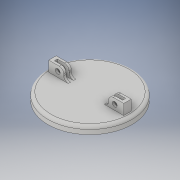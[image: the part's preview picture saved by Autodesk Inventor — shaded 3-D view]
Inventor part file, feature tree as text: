
AUTODESK INVENTOR PART (.ipt)
format: ipt  version: 2018.3 (Build 223284000, 284)  size: 182,272 bytes
history: native  units: in
note: dims shown in document units (in); Inventor stores cm internally (conversion verified against a paired STEP export)
features: extrude x3, sketch x3, fillet x2
ambient origin geometry x8: Origin, YZ Plane, XZ Plane, XY Plane, X Axis, Y Axis, Z Axis, Center Point
bodies: Solid1 (feature_tree)
feature tree (8):
  extrude  "Extrusion1"  Depth=1.4961in
  extrude  "Extrusion2"  Depth=1.9685in
  extrude  "Extrusion3"  Depth=1.7913in
  fillet  "Fillet1"  Radius=0.0787in
  fillet  "Fillet2"  Radius=0.1969in
  sketch  "Sketch1"  dims[d0=0.126in d1=1.4961in]
  sketch  "Sketch2"  dims[d2=0.2756in d3=1.9685in]
  sketch  "Sketch3"  dims[d4=0.1969in d5=0.0in d6=1.7913in d7=0.0787in d8=0.1969in d9=0.0in d10=2.2047in d11=0.1969in d12=0.0in d13=1.1811in d14=0.1181in d15=0.0787in]
